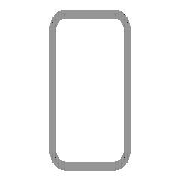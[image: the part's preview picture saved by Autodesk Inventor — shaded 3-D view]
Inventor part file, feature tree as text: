
AUTODESK INVENTOR PART (.ipt)
format: ipt  version: 2022 (Build 260153000, 153)  size: 147,456 bytes
history: native  units: mm (DEFAULTED — no unit token found)
features: other x3, sketch x3, extrude x1, plane x1
ambient origin geometry x8: Origin, YZ Plane, XZ Plane, XY Plane, X Axis, Y Axis, Z Axis, Center Point
bodies: Solid1 (feature_tree)
feature tree (8):
  other  "Driven Length"
  other  "Plano inicial"
  other  "Plano final"
  extrude  "Cuerpo"  Depth=20.0mm
  sketch  "Boceto1"  dims[d4=0.0mm d8=20.0mm]
  sketch  "Sketch2"  dims[d9=30.0mm]
  plane  "Work Plane3"
  sketch  "Sketch3"  dims[d10=2.9mm d11=-0.0mm d12=1400.0mm d13=90.0deg d14=1400.0mm]
